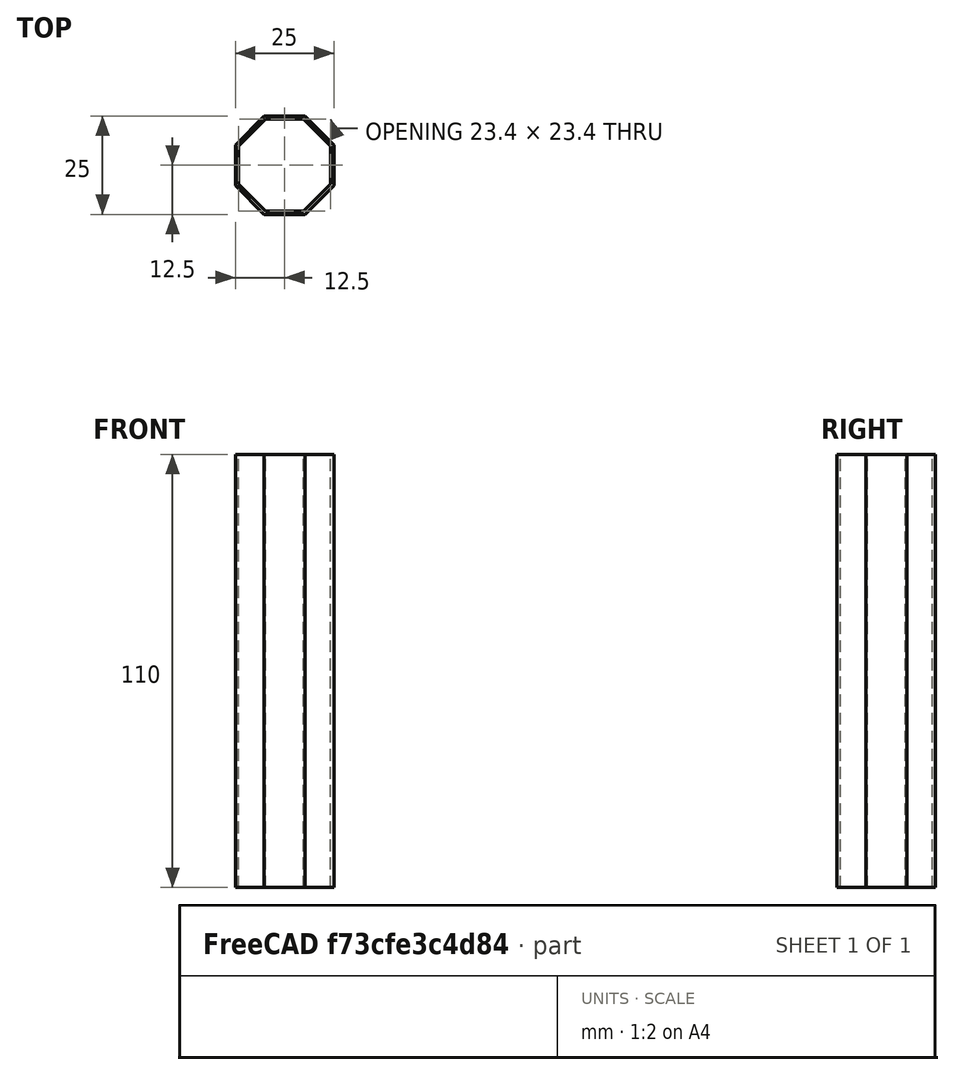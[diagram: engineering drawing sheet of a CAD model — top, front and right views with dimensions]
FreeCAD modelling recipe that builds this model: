
FCSTD DOCUMENT  (FreeCAD 0.18R14995 (Git))
Label: ZPillar
License: All rights reserved
LicenseURL: http://en.wikipedia.org/wiki/All_rights_reserved
objects: Sketcher::SketchObject×1, PartDesign::Pad×1, PartDesign::Body×1, App::Part×1
note: 4 computed .brp shape members not serialized (recipe doc carries the construction recipe); baked Part::Feature solids carry a one-line shape summary decoded from their .brp

FEATURE [Sketcher::SketchObject] Sketch  label="BaseSketch"
  MapMode = 5
  Support = -> [XY_Plane001]
  sketch-geometry (18):
    g0: LineSegment StartX=11.7 StartY=-4.8463 StartZ=0 EndX=11.7 EndY=4.8463 EndZ=0
    g1: LineSegment StartX=11.7 StartY=4.8463 StartZ=0 EndX=4.8463 EndY=11.7 EndZ=0
    g2: LineSegment StartX=4.8463 StartY=11.7 StartZ=0 EndX=-4.8463 EndY=11.7 EndZ=0
    g3: LineSegment StartX=-4.8463 StartY=11.7 StartZ=0 EndX=-11.7 EndY=4.8463 EndZ=0
    g4: LineSegment StartX=-11.7 StartY=4.8463 StartZ=0 EndX=-11.7 EndY=-4.8463 EndZ=0
    g5: LineSegment StartX=-11.7 StartY=-4.8463 StartZ=0 EndX=-4.8463 EndY=-11.7 EndZ=0
    g6: LineSegment StartX=-4.8463 StartY=-11.7 StartZ=0 EndX=4.8463 EndY=-11.7 EndZ=0
    g7: LineSegment StartX=4.8463 StartY=-11.7 StartZ=0 EndX=11.7 EndY=-4.8463 EndZ=0
    g8: Circle [constr] CenterX=0 CenterY=0 CenterZ=0 NormalX=0 NormalY=0 NormalZ=1 AngleXU=0 Radius=12.664
    g9: LineSegment StartX=-12.5 StartY=5.17767 StartZ=0 EndX=-12.5 EndY=-5.17767 EndZ=0
    g10: LineSegment StartX=-12.5 StartY=-5.17767 StartZ=0 EndX=-5.17767 EndY=-12.5 EndZ=0
    g11: LineSegment StartX=-5.17767 StartY=-12.5 StartZ=0 EndX=5.17767 EndY=-12.5 EndZ=0
    g12: LineSegment StartX=5.17767 StartY=-12.5 StartZ=0 EndX=12.5 EndY=-5.17767 EndZ=0
    g13: LineSegment StartX=12.5 StartY=-5.17767 StartZ=0 EndX=12.5 EndY=5.17767 EndZ=0
    g14: LineSegment StartX=12.5 StartY=5.17767 StartZ=0 EndX=5.17767 EndY=12.5 EndZ=0
    g15: LineSegment StartX=5.17767 StartY=12.5 StartZ=0 EndX=-5.17767 EndY=12.5 EndZ=0
    g16: LineSegment StartX=-5.17767 StartY=12.5 StartZ=0 EndX=-12.5 EndY=5.17767 EndZ=0
    g17: Circle [constr] CenterX=0 CenterY=0 CenterZ=0 NormalX=0 NormalY=0 NormalZ=1 AngleXU=0 Radius=13.5299
  constraints (40):
    c: Coincident(g0,g1)
    c: Coincident(g1,g2)
    c: Coincident(g2,g3)
    c: Coincident(g3,g4)
    c: Coincident(g4,g5)
    c: Coincident(g5,g6)
    c: Coincident(g6,g7)
    c: Coincident(g7,g0)
    c: Equal(g0, g1-g7) x7
    c: PointOnObject(g0,g8)
    c: PointOnObject(g1,g8)
    c: PointOnObject(g2,g8)
    c: PointOnObject(g3,g8)
    c: PointOnObject(g4,g8)
    c: PointOnObject(g5,g8)
    c: PointOnObject(g6,g8)
    c: PointOnObject(g7,g8)
    c: Coincident(g8,g-1)
    c: Vertical(g0)
    c: Coincident(g9,g10)
    c: Coincident(g10,g11)
    c: Coincident(g11,g12)
    c: Coincident(g12,g13)
    c: Coincident(g13,g14)
    c: Coincident(g14,g15)
    c: Coincident(g15,g16)
    c: Coincident(g16,g9)
    c: Equal(g9, g10-g16) x7
    c: PointOnObject(g9,g17)
    c: PointOnObject(g10,g17)
    c: PointOnObject(g11,g17)
    c: PointOnObject(g12,g17)
    c: PointOnObject(g13,g17)
    c: PointOnObject(g14,g17)
    c: PointOnObject(g15,g17)
    c: PointOnObject(g16,g17)
    c: Coincident(g17,g-1)
    c: Vertical(g9)
    c: Distance(g9,g4) = 0.8
    c: Distance(g9,g13) = 25
FEATURE [PartDesign::Pad] Pad  label="BasePad"
  Length = 110
  Length2 = 100
  Profile = -> Sketch
  Type = 0
FEATURE [PartDesign::Body] Body  label="ZPillarPartBody"
  Group = -> [Sketch,Pad]
  Origin = -> Origin001
  Tip = -> Pad
FEATURE [App::Part] Part  label="ZPillarPart"
  Group = -> [Body]
  License = CC BY 3.0
  LicenseURL = http://creativecommons.org/licenses/by/3.0/
  Origin = -> Origin
